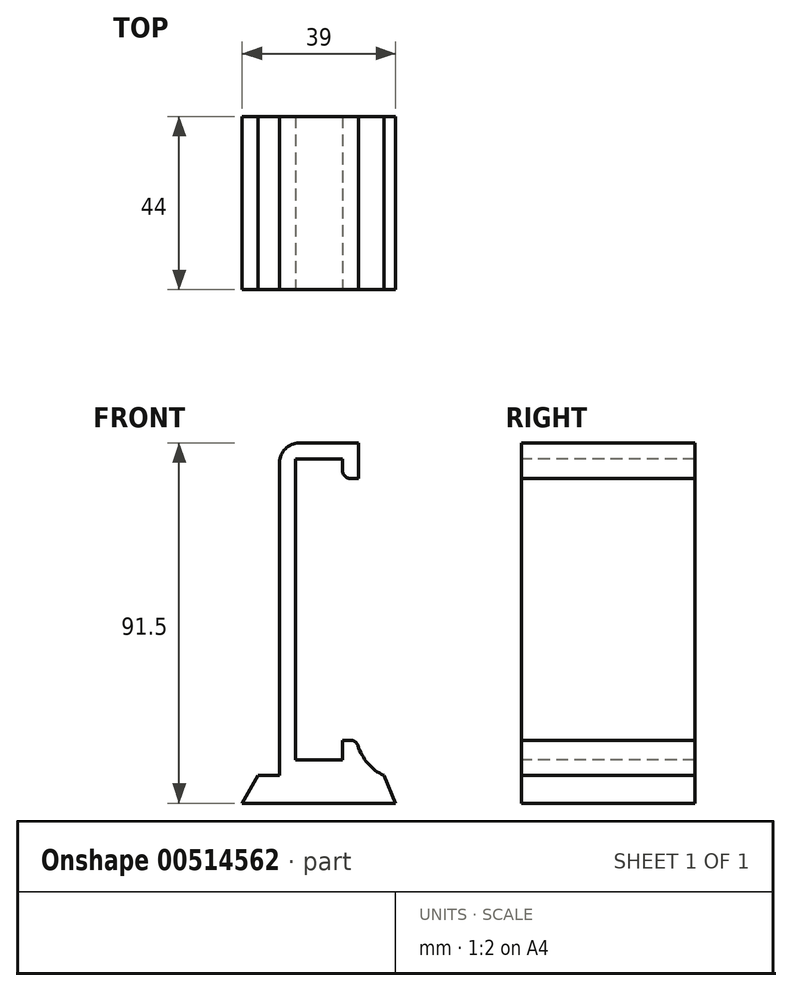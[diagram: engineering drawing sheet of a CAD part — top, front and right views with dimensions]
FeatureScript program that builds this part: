
annotation { "Feature Type Name" : "Feature", "Feature Type Description" : "" }
export const myFeature = defineFeature(function(context is Context, id is Id, definition is map)
    precondition{}
    {
        {
            var Q0;
            Q0=qCreatedBy(makeId("Top.planeOp"),FACE);
            var sketch = newSketch(context, id + "F0", { "sketchPlane" : qUnion([Q0])});
            skLineSegment(sketch, "E0.bottom", {"start": v(19.5, 22) * mm, "end": v(-19.5, 22) * mm});
            skLineSegment(sketch, "E0.top", {"start": v(19.5, -22) * mm, "end": v(-19.5, -22) * mm});
            skLineSegment(sketch, "E0.left", {"start": v(19.5, 22) * mm, "end": v(19.5, -22) * mm});
            skLineSegment(sketch, "E0.right", {"start": v(-19.5, 22) * mm, "end": v(-19.5, -22) * mm});
            skPoint(sketch, "E0.middle", {"position": v(0, 0) * mm});
            skSolve(sketch);
        }
        {
            var Q0;
            Q0=makeQuery(id+"F0.imprint","IMPRINT",FACE,{"disambiguationData":[TD([[makeQuery(id+"F0.imprint","IMPRINT",EDGE,{"derivedFrom":sQuery(id+"F0.wireOp",EDGE,"E0.bottom")}),1.0]])]});
            extrude(context, id + "F1", {"entities" : qUnion([Q0]), "depth" : 7 * mm});
        }
        {
            var Q0;
            Q0=makeQuery(id+"F1.opExtrude","SWEPT_FACE",FACE,{"disambiguationData":[OSD([sQuery(id+"F0.wireOp",EDGE,"E0.top")])]});
            var sketch = newSketch(context, id + "F2", { "sketchPlane" : qUnion([Q0])});
            skLineSegment(sketch, "E1", {"start": v(-19.5, 0) * mm, "end": v(-15.5, 7) * mm});
            skLineSegment(sketch, "E2", {"start": v(19.5, 0) * mm, "end": v(16.5, 7) * mm});
            skSolve(sketch);
        }
        {
            var Q0;
            {var subQ0=sQuery(id+"F2.wireOp",EDGE,"E1");Q0=makeQuery(id+"F2.imprint","IMPRINT",FACE,{"disambiguationData":[TD([[makeQuery(id+"F2.imprint","IMPRINT",EDGE,{"derivedFrom":subQ0}),1.0]])]});}
            var Q1;
            {var subQ0=sQuery(id+"F2.wireOp",EDGE,"E2");Q1=makeQuery(id+"F2.imprint","IMPRINT",FACE,{"disambiguationData":[TD([[makeQuery(id+"F2.imprint","IMPRINT",EDGE,{"derivedFrom":subQ0}),-1.0]])]});}
            extrude(context, id + "F3", {"entities" : qUnion([Q0, Q1]), "operationType" : NewBodyOperationType.REMOVE, "oppositeDirection" : true, "depth" : 44 * mm, "offsetDistance" : 25 * mm});
        }
        {
            var Q0;
            Q0=makeQuery(id+"F1.opExtrude","CAP_FACE",FACE,{"disambiguationData":[OSD([sQuery(id+"F0.wireOp",EDGE,"E0.bottom"),sQuery(id+"F0.wireOp",EDGE,"E0.top"),sQuery(id+"F0.wireOp",EDGE,"E0.left"),sQuery(id+"F0.wireOp",EDGE,"E0.right")])],"isStart":false});
            var sketch = newSketch(context, id + "F4", { "sketchPlane" : qUnion([Q0])});
            skLineSegment(sketch, "E3.bottom", {"start": v(10, 22) * mm, "end": v(-10, 22) * mm});
            skLineSegment(sketch, "E3.top", {"start": v(10, -22) * mm, "end": v(-10, -22) * mm});
            skLineSegment(sketch, "E3.left", {"start": v(10, 22) * mm, "end": v(10, -22) * mm});
            skLineSegment(sketch, "E3.right", {"start": v(-10, 22) * mm, "end": v(-10, -22) * mm});
            skPoint(sketch, "E3.middle", {"position": v(0, 0) * mm});
            skSolve(sketch);
        }
        {
            var Q0;
            Q0=makeQuery(id+"F4.imprint","IMPRINT",FACE,{"disambiguationData":[TD([[makeQuery(id+"F4.imprint","IMPRINT",EDGE,{"derivedFrom":sQuery(id+"F4.wireOp",EDGE,"E3.bottom")}),1.0]])]});
            extrude(context, id + "F5", {"entities" : qUnion([Q0]), "operationType" : NewBodyOperationType.ADD, "depth" : 5 * mm});
        }
        {
            var Q0;
            Q0=makeQuery(id+"F5.opExtrude","CAP_FACE",FACE,{"disambiguationData":[OSD([sQuery(id+"F4.wireOp",EDGE,"E3.bottom"),sQuery(id+"F4.wireOp",EDGE,"E3.top"),sQuery(id+"F4.wireOp",EDGE,"E3.left"),sQuery(id+"F4.wireOp",EDGE,"E3.right")])],"isStart":false});
            var sketch = newSketch(context, id + "F6", { "sketchPlane" : qUnion([Q0])});
            skSolve(sketch);
        }
        {
            var Q0;
            Q0=makeQuery(id+"F6.imprint","IMPRINT",FACE,{"disambiguationData":[TD([[makeQuery(id+"F6.imprint","IMPRINT",EDGE,{"derivedFrom":makeQuery(id+"F5.opExtrude","CAP_EDGE",EDGE,{"disambiguationData":[OSD([sQuery(id+"F4.wireOp",EDGE,"E3.bottom")])],"isStart":false})}),1.0]])]});
            extrude(context, id + "F7", {"entities" : qUnion([Q0]), "operationType" : NewBodyOperationType.ADD, "depth" : 79.5 * mm, "offsetDistance" : 25 * mm});
        }
        {
            var Q0;
            {var subQ0=sQuery(id+"F4.wireOp",EDGE,"E3.top");Q0=makeQuery(id+"F7.boolean.opBoolean","MERGE",FACE,{"derivedFrom":[makeQuery(id+"F5.boolean.opBoolean","MERGE",FACE,{"derivedFrom":[makeQuery(id+"F1.opExtrude","SWEPT_FACE",FACE,{"disambiguationData":[OSD([sQuery(id+"F0.wireOp",EDGE,"E0.top")])]}),makeQuery(id+"F5.opExtrude","SWEPT_FACE",FACE,{"disambiguationData":[OSD([subQ0])]})]}),makeQuery(id+"F7.opExtrude","SWEPT_FACE",FACE,{"disambiguationData":[OSD([subQ0])]})]});}
            var sketch = newSketch(context, id + "F8", { "sketchPlane" : qUnion([Q0])});
            skLineSegment(sketch, "E4.bottom", {"start": v(6, 87.5) * mm, "end": v(-6, 87.5) * mm});
            skLineSegment(sketch, "E4.top", {"start": v(6, 11) * mm, "end": v(-6, 11) * mm});
            skLineSegment(sketch, "E4.left", {"start": v(6, 87.5) * mm, "end": v(6, 11) * mm});
            skLineSegment(sketch, "E4.right", {"start": v(-6, 87.5) * mm, "end": v(-6, 11) * mm});
            skPoint(sketch, "E4.middle", {"position": v(0, 49.25) * mm});
            skSolve(sketch);
        }
        {
            var Q0;
            Q0=makeQuery(id+"F8.imprint","IMPRINT",FACE,{"disambiguationData":[TD([[makeQuery(id+"F8.imprint","IMPRINT",EDGE,{"derivedFrom":sQuery(id+"F8.wireOp",EDGE,"E4.bottom")}),1.0]])]});
            extrude(context, id + "F9", {"entities" : qUnion([Q0]), "operationType" : NewBodyOperationType.REMOVE, "oppositeDirection" : true, "depth" : 44 * mm, "offsetDistance" : 25 * mm});
        }
        {
            var Q0;
            {var subQ0=sQuery(id+"F4.wireOp",EDGE,"E3.top");Q0=makeQuery(id+"F7.boolean.opBoolean","MERGE",FACE,{"derivedFrom":[makeQuery(id+"F5.boolean.opBoolean","MERGE",FACE,{"derivedFrom":[makeQuery(id+"F1.opExtrude","SWEPT_FACE",FACE,{"disambiguationData":[OSD([sQuery(id+"F0.wireOp",EDGE,"E0.top")])]}),makeQuery(id+"F5.opExtrude","SWEPT_FACE",FACE,{"disambiguationData":[OSD([subQ0])]})]}),makeQuery(id+"F7.opExtrude","SWEPT_FACE",FACE,{"disambiguationData":[OSD([subQ0])]})]});}
            var sketch = newSketch(context, id + "F10", { "sketchPlane" : qUnion([Q0])});
            skLineSegment(sketch, "E5", {"start": v(6, 82.5) * mm, "end": v(10, 82.5) * mm});
            skLineSegment(sketch, "E6", {"start": v(6, 16) * mm, "end": v(10, 16) * mm});
            skSolve(sketch);
        }
        {
            var Q0;
            {var subQ0=sQuery(id+"F10.wireOp",EDGE,"E5");Q0=makeQuery(id+"F10.imprint","IMPRINT",FACE,{"disambiguationData":[TD([[makeQuery(id+"F10.imprint","IMPRINT",EDGE,{"derivedFrom":subQ0}),-1.0]])]});}
            extrude(context, id + "F11", {"entities" : qUnion([Q0]), "operationType" : NewBodyOperationType.REMOVE, "oppositeDirection" : true, "depth" : 44 * mm, "offsetDistance" : 25 * mm});
        }
        {
            var Q0;
            Q0=makeQuery(id+"F11.boolean.opBoolean","COPY",EDGE,{"derivedFrom":makeQuery(id+"F11.opExtrude","SWEPT_EDGE",EDGE,{"disambiguationData":[OSD([sQuery(id+"F4.wireOp",EDGE,"E3.top"),sQuery(id+"F4.wireOp",EDGE,"E3.left"),sQuery(id+"F10.wireOp",EDGE,"E5")])]})});
            var Q1;
            Q1=makeQuery(id+"F11.boolean.opBoolean","COPY",EDGE,{"derivedFrom":makeQuery(id+"F11.opExtrude","SWEPT_EDGE",EDGE,{"disambiguationData":[OSD([sQuery(id+"F8.wireOp",EDGE,"E4.left"),sQuery(id+"F10.wireOp",EDGE,"E6")])]})});
            var Q2;
            Q2=makeQuery(id+"F11.boolean.opBoolean","COPY",EDGE,{"derivedFrom":makeQuery(id+"F11.opExtrude","SWEPT_EDGE",EDGE,{"disambiguationData":[OSD([sQuery(id+"F4.wireOp",EDGE,"E3.top"),sQuery(id+"F4.wireOp",EDGE,"E3.left"),sQuery(id+"F10.wireOp",EDGE,"E6")])]})});
            var Q3;
            Q3=makeQuery(id+"F11.boolean.opBoolean","COPY",EDGE,{"derivedFrom":makeQuery(id+"F11.opExtrude","SWEPT_EDGE",EDGE,{"disambiguationData":[OSD([sQuery(id+"F8.wireOp",EDGE,"E4.left"),sQuery(id+"F10.wireOp",EDGE,"E5")])]})});
            fillet(context, id + "F12", {"entities" : qUnion([Q0, Q1, Q2, Q3]), "radius" : 2 * mm, "tangentPropagation" : true, "allowEdgeOverflow" : false});
        }
        {
            var Q0;
            Q0=makeQuery(id+"F5.opExtrude","CAP_EDGE",EDGE,{"disambiguationData":[OSD([sQuery(id+"F4.wireOp",EDGE,"E3.left")])],"isStart":true});
            var Q1;
            Q1=makeQuery(id+"F5.opExtrude","CAP_EDGE",EDGE,{"disambiguationData":[OSD([sQuery(id+"F4.wireOp",EDGE,"E3.right")])],"isStart":true});
            fillet(context, id + "F13", {"entities" : qUnion([Q0, Q1]), "radius" : 13 * mm, "tangentPropagation" : true, "allowEdgeOverflow" : false});
        }
        {
            var Q0;
            Q0=makeQuery(id+"F7.opExtrude","CAP_EDGE",EDGE,{"disambiguationData":[OSD([sQuery(id+"F4.wireOp",EDGE,"E3.right")])],"isStart":false});
            fillet(context, id + "F14", {"entities" : qUnion([Q0]), "radius" : 5 * mm, "tangentPropagation" : true, "allowEdgeOverflow" : false});
        }
    });
